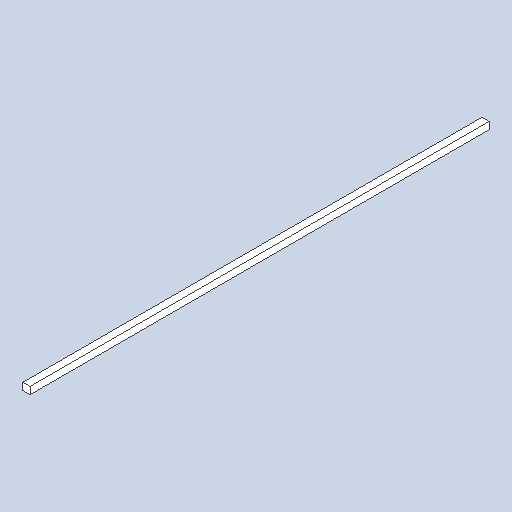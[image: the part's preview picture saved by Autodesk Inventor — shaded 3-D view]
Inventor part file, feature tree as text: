
AUTODESK INVENTOR PART (.ipt)
format: ipt  version: 2023 (Build 270158000, 158)  size: 96,768 bytes
history: native  units: in
note: dims shown in document units (in); Inventor stores cm internally (conversion verified against a paired STEP export)
features: extrude x1, sketch x1
ambient origin geometry x8: Origin, YZ Plane, XZ Plane, XY Plane, X Axis, Y Axis, Z Axis, Center Point
bodies: Solid1 (feature_tree)
feature tree (2):
  extrude  "Extrusion1"  Depth=0.1875in
  sketch  "Sketch1"  dims[d0=0.1875in d1=0.1875in d2=12.0in d3=0.0in]
